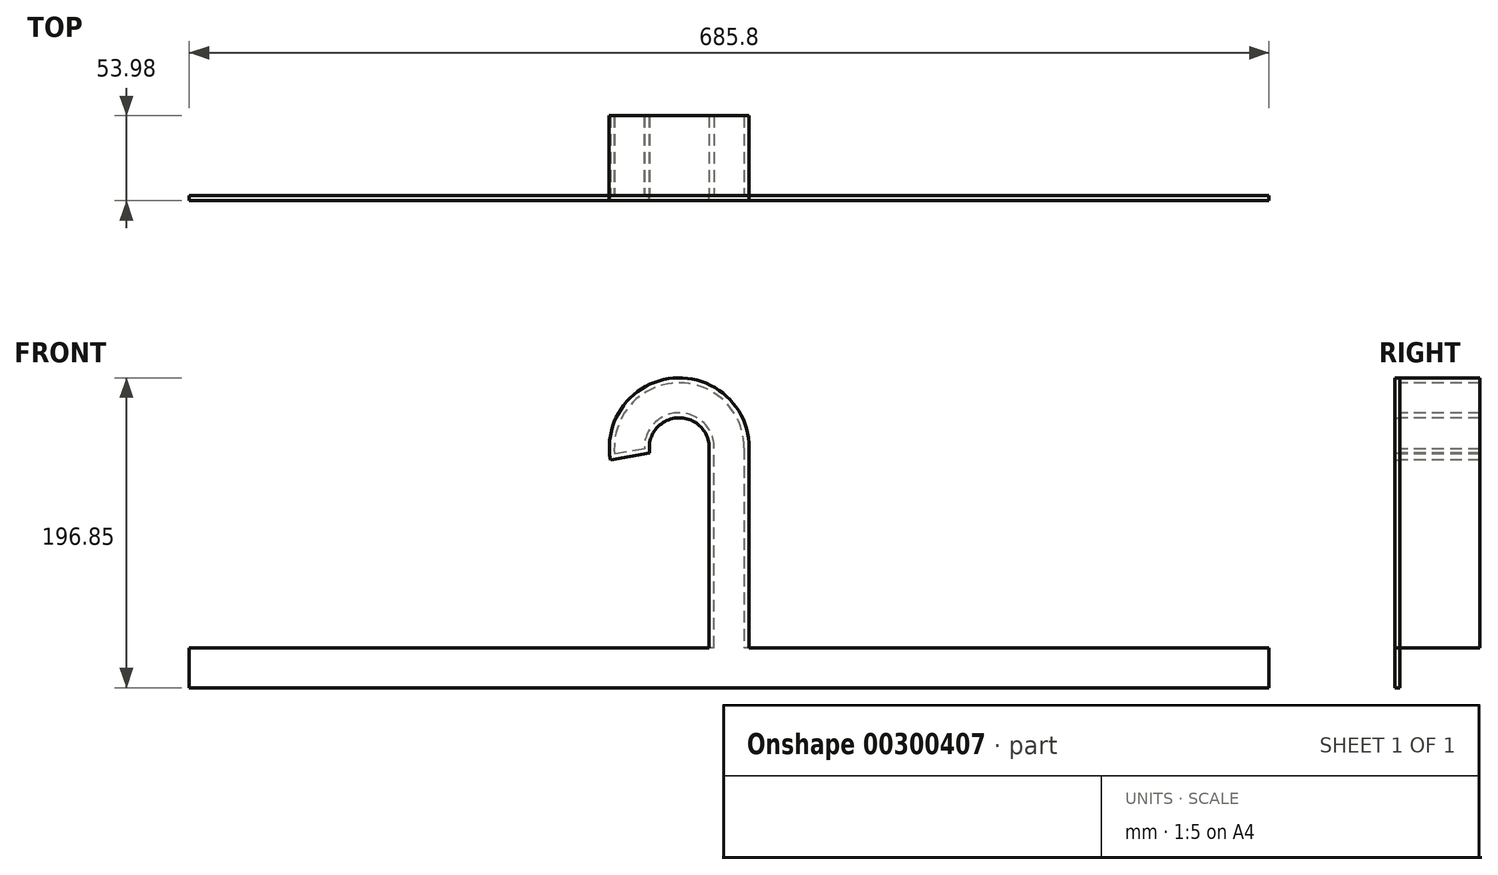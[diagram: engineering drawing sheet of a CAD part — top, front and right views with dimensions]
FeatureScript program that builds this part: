
annotation { "Feature Type Name" : "Feature", "Feature Type Description" : "" }
export const myFeature = defineFeature(function(context is Context, id is Id, definition is map)
    precondition{}
    {
        {
            var Q0;
            Q0=qCreatedBy(makeId("Front.planeOp"),FACE);
            var sketch = newSketch(context, id + "F0", { "sketchPlane" : qUnion([Q0])});
            skLineSegment(sketch, "E0.bottom", {"start": v(12.7, 63.5) * mm, "end": v(-12.7, 63.5) * mm});
            skLineSegment(sketch, "E0.top", {"start": v(12.7, -63.5) * mm, "end": v(-12.7, -63.5) * mm});
            skLineSegment(sketch, "E0.left", {"start": v(12.7, 63.5) * mm, "end": v(12.7, -63.5) * mm});
            skLineSegment(sketch, "E0.right", {"start": v(-12.7, 63.5) * mm, "end": v(-12.7, -63.5) * mm});
            skPoint(sketch, "E0.middle", {"position": v(0, 0) * mm});
            skSolve(sketch);
        }
        {
            var Q0;
            Q0=makeQuery(id+"F0.imprint","IMPRINT",FACE,{"disambiguationData":[TD([[makeQuery(id+"F0.imprint","IMPRINT",EDGE,{"derivedFrom":sQuery(id+"F0.wireOp",EDGE,"E0.bottom")}),1.0]])]});
            extrude(context, id + "F1", {"entities" : qUnion([Q0]), "endBound" : BoundingType.SYMMETRIC, "depth" : 3.17 * mm});
        }
        {
            var Q0;
            Q0=makeQuery(id+"F1.opExtrude","SWEPT_FACE",FACE,{"disambiguationData":[OSD([sQuery(id+"F0.wireOp",EDGE,"E0.bottom")])]});
            var sketch = newSketch(context, id + "F2", { "sketchPlane" : qUnion([Q0])});
            skLineSegment(sketch, "E1", {"start": v(-31.75, 12.7) * mm, "end": v(-31.75, -1.59) * mm});
            skSolve(sketch);
        }
        {
            var Q0;
            {var subQ0=sQuery(id+"F0.wireOp",EDGE,"E0.bottom");Q0=makeQuery(id+"F2.imprint","IMPRINT",FACE,{"disambiguationData":[TD([[makeQuery(id+"F2.imprint","IMPRINT",EDGE,{"derivedFrom":makeQuery(id+"F1.opExtrude","CAP_EDGE",EDGE,{"disambiguationData":[OSD([subQ0])],"isStart":true})}),1.0]])]});}
            var Q1;
            Q1=sQuery(id+"F2.wireOp",EDGE,"E1");
            revolve(context, id + "F3", {"operationType" : NewBodyOperationType.ADD, "entities" : qUnion([Q0]), "axis" : qUnion([Q1]), "revolveType" : RevolveType.ONE_DIRECTION, "angle" : 190 * degree});
        }
        {
            var Q0;
            {var subQ0=sQuery(id+"F0.wireOp",EDGE,"E0.bottom");Q0=makeQuery(id+"F3.boolean.opBoolean","MERGE",FACE,{"derivedFrom":[makeQuery(id+"F1.opExtrude","CAP_FACE",FACE,{"disambiguationData":[OSD([subQ0,sQuery(id+"F0.wireOp",EDGE,"E0.top"),sQuery(id+"F0.wireOp",EDGE,"E0.left"),sQuery(id+"F0.wireOp",EDGE,"E0.right")])],"isStart":false}),makeQuery(id+"F3.opRevolve","SWEPT_FACE",FACE,{"disambiguationData":[OSD([subQ0]),TDD([makeQuery(id+"F2.imprint","IMPRINT",EDGE,{"derivedFrom":makeQuery(id+"F1.opExtrude","CAP_EDGE",EDGE,{"disambiguationData":[OSD([subQ0])],"isStart":false})})])]})]});}
            var sketch = newSketch(context, id + "F4", { "sketchPlane" : qUnion([Q0])});
            skLineSegment(sketch, "E2.bottom", {"start": v(0, -63.5) * mm, "end": v(342.9, -63.5) * mm});
            skLineSegment(sketch, "E2.top", {"start": v(0, -88.9) * mm, "end": v(342.9, -88.9) * mm});
            skLineSegment(sketch, "E2.left", {"start": v(0, -63.5) * mm, "end": v(0, -88.9) * mm});
            skLineSegment(sketch, "E2.right", {"start": v(342.9, -63.5) * mm, "end": v(342.9, -88.9) * mm});
            skSolve(sketch);
        }
        {
            var Q0;
            Q0 = qSketchRegion(id + "F4", true);
            extrude(context, id + "F5", {"entities" : qUnion([Q0]), "operationType" : NewBodyOperationType.ADD, "oppositeDirection" : true, "depth" : 3.17 * mm});
        }
        {
            var Q0;
            {var subQ0=sQuery(id+"F0.wireOp",EDGE,"E0.bottom");Q0=makeQuery(id+"F5.boolean.opBoolean","MERGE",FACE,{"derivedFrom":[makeQuery(id+"F3.boolean.opBoolean","MERGE",FACE,{"derivedFrom":[makeQuery(id+"F1.opExtrude","CAP_FACE",FACE,{"disambiguationData":[OSD([subQ0,sQuery(id+"F0.wireOp",EDGE,"E0.top"),sQuery(id+"F0.wireOp",EDGE,"E0.left"),sQuery(id+"F0.wireOp",EDGE,"E0.right")])],"isStart":false}),makeQuery(id+"F3.opRevolve","SWEPT_FACE",FACE,{"disambiguationData":[OSD([subQ0]),TDD([makeQuery(id+"F2.imprint","IMPRINT",EDGE,{"derivedFrom":makeQuery(id+"F1.opExtrude","CAP_EDGE",EDGE,{"disambiguationData":[OSD([subQ0])],"isStart":false})})])]})]}),makeQuery(id+"F5.opExtrude","CAP_FACE",FACE,{"disambiguationData":[OSD([sQuery(id+"F4.wireOp",EDGE,"E2.bottom"),sQuery(id+"F4.wireOp",EDGE,"E2.top"),sQuery(id+"F4.wireOp",EDGE,"E2.left"),sQuery(id+"F4.wireOp",EDGE,"E2.right")])],"isStart":true})]});}
            var sketch = newSketch(context, id + "F6", { "sketchPlane" : qUnion([Q0])});
            skLineSegment(sketch, "E3.bottom", {"start": v(0, -63.5) * mm, "end": v(-342.9, -63.5) * mm});
            skLineSegment(sketch, "E3.top", {"start": v(0, -88.9) * mm, "end": v(-342.9, -88.9) * mm});
            skLineSegment(sketch, "E3.left", {"start": v(0, -63.5) * mm, "end": v(0, -88.9) * mm});
            skLineSegment(sketch, "E3.right", {"start": v(-342.9, -63.5) * mm, "end": v(-342.9, -88.9) * mm});
            skSolve(sketch);
        }
        {
            var Q0;
            Q0 = qSketchRegion(id + "F6", true);
            extrude(context, id + "F7", {"entities" : qUnion([Q0]), "operationType" : NewBodyOperationType.ADD, "oppositeDirection" : true, "depth" : 3.17 * mm});
        }
        {
            var Q0;
            {var subQ0=sQuery(id+"F0.wireOp",EDGE,"E0.bottom");Q0=makeQuery(id+"F7.boolean.opBoolean","MERGE",FACE,{"derivedFrom":[makeQuery(id+"F5.boolean.opBoolean","MERGE",FACE,{"derivedFrom":[makeQuery(id+"F3.boolean.opBoolean","MERGE",FACE,{"derivedFrom":[makeQuery(id+"F1.opExtrude","CAP_FACE",FACE,{"disambiguationData":[OSD([subQ0,sQuery(id+"F0.wireOp",EDGE,"E0.top"),sQuery(id+"F0.wireOp",EDGE,"E0.left"),sQuery(id+"F0.wireOp",EDGE,"E0.right")])],"isStart":true}),makeQuery(id+"F3.opRevolve","SWEPT_FACE",FACE,{"disambiguationData":[OSD([subQ0]),TDD([makeQuery(id+"F2.imprint","IMPRINT",EDGE,{"derivedFrom":makeQuery(id+"F1.opExtrude","CAP_EDGE",EDGE,{"disambiguationData":[OSD([subQ0])],"isStart":true})})])]})]}),makeQuery(id+"F5.opExtrude","CAP_FACE",FACE,{"disambiguationData":[OSD([sQuery(id+"F4.wireOp",EDGE,"E2.bottom"),sQuery(id+"F4.wireOp",EDGE,"E2.top"),sQuery(id+"F4.wireOp",EDGE,"E2.left"),sQuery(id+"F4.wireOp",EDGE,"E2.right")])],"isStart":false})]}),makeQuery(id+"F7.opExtrude","CAP_FACE",FACE,{"disambiguationData":[OSD([sQuery(id+"F6.wireOp",EDGE,"E3.bottom"),sQuery(id+"F6.wireOp",EDGE,"E3.top"),sQuery(id+"F6.wireOp",EDGE,"E3.left"),sQuery(id+"F6.wireOp",EDGE,"E3.right")])],"isStart":false})]});}
            var sketch = newSketch(context, id + "F8", { "sketchPlane" : qUnion([Q0])});
            skArc(sketch, "E4.0", {"start": v(75.52, 55.78) * mm, "mid": v(35.62, 107.78) * mm, "end": v(-12.7, 63.5) * mm});
            skPoint(sketch, "E5.0", {"position": v(50.51, 60.2) * mm});
            skLineSegment(sketch, "E6.0", {"start": v(75.52, 55.78) * mm, "end": v(50.51, 60.2) * mm});
            skArc(sketch, "E7.0", {"start": v(50.51, 60.2) * mm, "mid": v(33.41, 82.48) * mm, "end": v(12.7, 63.5) * mm});
            skLineSegment(sketch, "E8.0", {"start": v(12.7, 63.5) * mm, "end": v(12.7, -63.5) * mm});
            skLineSegment(sketch, "E9.0", {"start": v(-12.7, 63.5) * mm, "end": v(-12.7, -63.5) * mm});
            skLineSegment(sketch, "E10", {"start": v(-12.7, -63.5) * mm, "end": v(12.7, -63.5) * mm});
            skLineSegment(sketch, "E11.5", {"start": v(-9.53, 63.5) * mm, "end": v(-9.52, -63.5) * mm});
            skLineSegment(sketch, "E11.6", {"start": v(9.53, -63.5) * mm, "end": v(9.53, 63.5) * mm});
            skArc(sketch, "E11.7", {"start": v(9.53, 63.5) * mm, "mid": v(32.1, 85.72) * mm, "end": v(53.96, 62.8) * mm});
            skLineSegment(sketch, "E11.8", {"start": v(53.96, 62.8) * mm, "end": v(72.83, 59.48) * mm});
            skArc(sketch, "E11.9", {"start": v(72.83, 59.48) * mm, "mid": v(33.76, 104.73) * mm, "end": v(-9.52, 63.5) * mm});
            skPoint(sketch, "E12", {"position": v(9.53, -63.5) * mm});
            skPoint(sketch, "E13", {"position": v(-9.52, -63.5) * mm});
            skSolve(sketch);
        }
        {
            var Q0;
            Q0=makeQuery(id+"F8.imprint","IMPRINT",FACE,{"disambiguationData":[TD([[makeQuery(id+"F8.imprint","IMPRINT",EDGE,{"derivedFrom":sQuery(id+"F8.wireOp",EDGE,"E4.0")}),1.0]])]});
            extrude(context, id + "F9", {"entities" : qUnion([Q0]), "depth" : 50.8 * mm});
        }
    });
